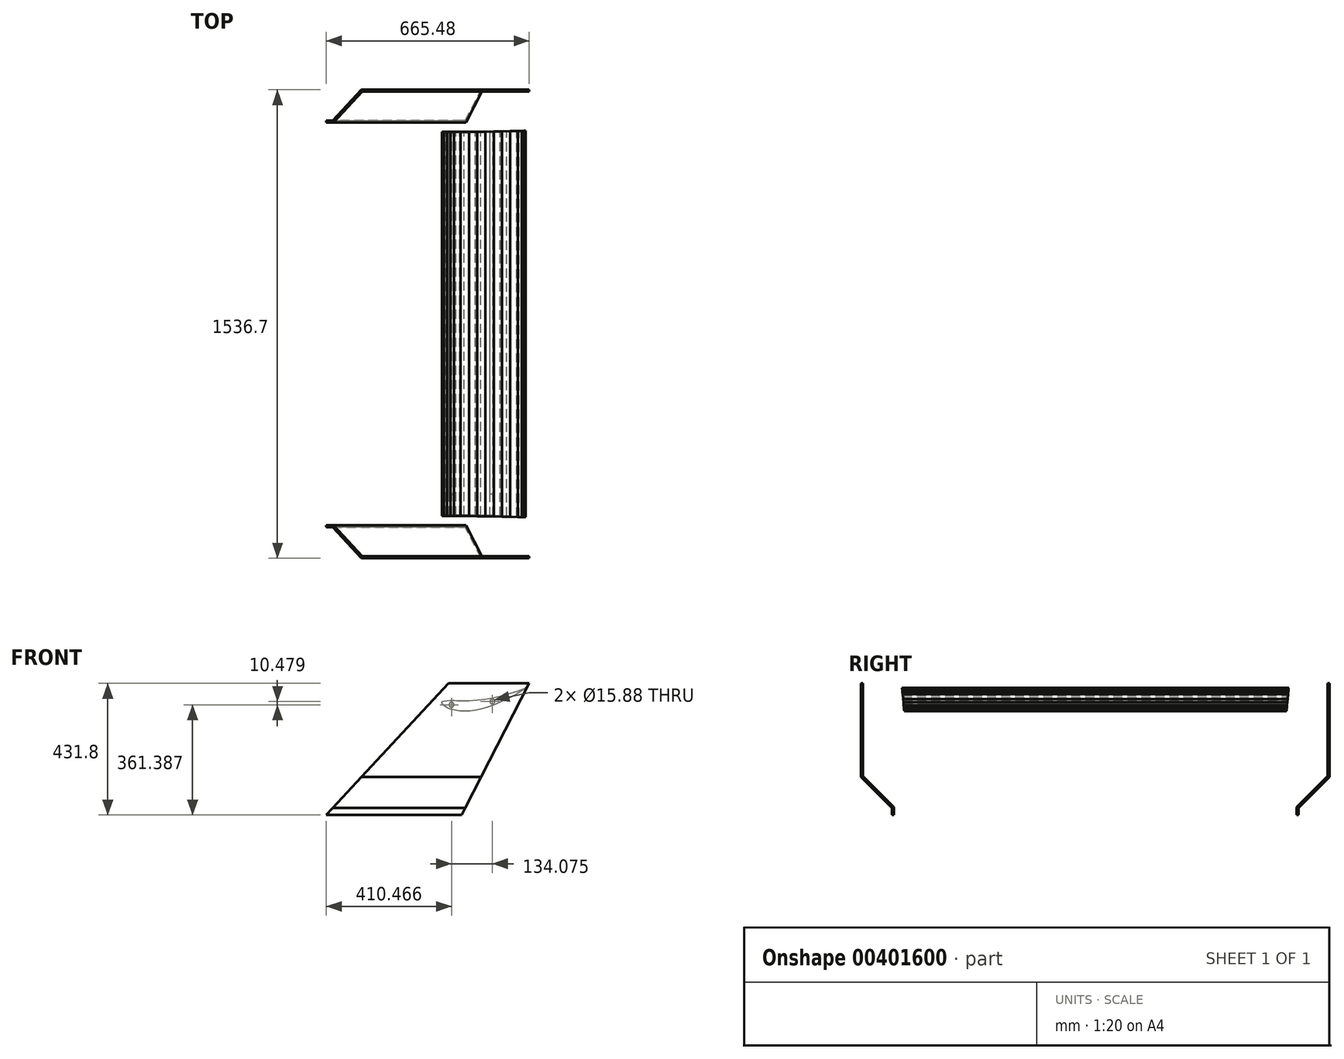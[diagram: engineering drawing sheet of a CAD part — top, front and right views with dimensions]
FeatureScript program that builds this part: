
annotation { "Feature Type Name" : "Feature", "Feature Type Description" : "" }
export const myFeature = defineFeature(function(context is Context, id is Id, definition is map)
    precondition{}
    {
        {
            var Q0;
            Q0=qCreatedBy(makeId("Front.planeOp"),FACE);
            var sketch = newSketch(context, id + "F0", { "sketchPlane" : qUnion([Q0])});
            skLineSegment(sketch, "E0.MirrorCS", {"start": v(175.68, 60.41) * mm, "end": v(175.68, 60.41) * mm});
            skLineSegment(sketch, "E1.MirrorCS", {"start": v(175.68, 60.41) * mm, "end": v(175.68, 60.4) * mm});
            skLineSegment(sketch, "E2.MirrorCS", {"start": v(175.68, 60.4) * mm, "end": v(175.68, 60.4) * mm});
            skLineSegment(sketch, "E3.MirrorCS", {"start": v(175.68, 60.4) * mm, "end": v(175.67, 60.4) * mm});
            skLineSegment(sketch, "E4.MirrorCS", {"start": v(175.67, 60.4) * mm, "end": v(175.63, 60.36) * mm});
            skLineSegment(sketch, "E5.MirrorCS", {"start": v(175.63, 60.36) * mm, "end": v(175.52, 60.28) * mm});
            skLineSegment(sketch, "E6.MirrorCS", {"start": v(175.52, 60.28) * mm, "end": v(175.2, 60.07) * mm});
            skLineSegment(sketch, "E7.MirrorCS", {"start": v(175.2, 60.07) * mm, "end": v(174.57, 59.64) * mm});
            skLineSegment(sketch, "E8.MirrorCS", {"start": v(175.58, 60.37) * mm, "end": v(175.66, 60.4) * mm});
            skLineSegment(sketch, "E9.MirrorCS", {"start": v(174.57, 59.64) * mm, "end": v(173.65, 58.98) * mm});
            skLineSegment(sketch, "E10.MirrorCS", {"start": v(175.22, 60.2) * mm, "end": v(175.58, 60.37) * mm});
            skLineSegment(sketch, "E11.MirrorCS", {"start": v(175.66, 60.4) * mm, "end": v(175.68, 60.41) * mm});
            skLineSegment(sketch, "E12.MirrorCS", {"start": v(174.2, 59.69) * mm, "end": v(175.22, 60.2) * mm});
            skLineSegment(sketch, "E13.MirrorCS", {"start": v(-99.43, 13.1) * mm, "end": v(-99.05, 14.17) * mm});
            skLineSegment(sketch, "E14.MirrorCS", {"start": v(-99.46, 11.96) * mm, "end": v(-99.43, 13.1) * mm});
            skLineSegment(sketch, "E15.MirrorCS", {"start": v(173.65, 58.98) * mm, "end": v(172.07, 57.7) * mm});
            skLineSegment(sketch, "E16.MirrorCS", {"start": v(172.07, 57.7) * mm, "end": v(168.47, 54.76) * mm});
            skLineSegment(sketch, "E17.MirrorCS", {"start": v(169.51, 57.67) * mm, "end": v(172.47, 58.9) * mm});
            skLineSegment(sketch, "E18.MirrorCS", {"start": v(-99.05, 14.17) * mm, "end": v(-97.26, 15.57) * mm});
            skLineSegment(sketch, "E19.MirrorCS", {"start": v(-97.14, 6.38) * mm, "end": v(-98.65, 9.03) * mm});
            skLineSegment(sketch, "E20.MirrorCS", {"start": v(172.47, 58.9) * mm, "end": v(174.2, 59.69) * mm});
            skLineSegment(sketch, "E21.MirrorCS", {"start": v(-97.26, 15.57) * mm, "end": v(-93, 17.2) * mm});
            skLineSegment(sketch, "E22.MirrorCS", {"start": v(-98.65, 9.03) * mm, "end": v(-99.46, 11.96) * mm});
            skLineSegment(sketch, "E23.MirrorCS", {"start": v(-95.22, 4) * mm, "end": v(-97.14, 6.38) * mm});
            skLineSegment(sketch, "E24.MirrorCS", {"start": v(150.15, 50.38) * mm, "end": v(163, 55.07) * mm});
            skLineSegment(sketch, "E25.MirrorCS", {"start": v(-49.22, 18.5) * mm, "end": v(-38.24, 18.2) * mm});
            skLineSegment(sketch, "E26.MirrorCS", {"start": v(-53.7, -13.81) * mm, "end": v(-67.02, -10.8) * mm});
            skLineSegment(sketch, "E27.MirrorCS", {"start": v(68.4, 3.21) * mm, "end": v(45.5, -5.16) * mm});
            skLineSegment(sketch, "E28.MirrorCS", {"start": v(163, 55.07) * mm, "end": v(169.51, 57.67) * mm});
            skLineSegment(sketch, "E29.MirrorCS", {"start": v(168.47, 54.76) * mm, "end": v(161.17, 49.3) * mm});
            skLineSegment(sketch, "E30.MirrorCS", {"start": v(161.17, 49.3) * mm, "end": v(153.4, 44.44) * mm});
            skLineSegment(sketch, "E31.MirrorCS", {"start": v(153.4, 44.44) * mm, "end": v(145.45, 39.92) * mm});
            skCircle(sketch, "E32.MirrorC", {"center": v(-67.77, 4.73) * mm, "radius": 7.94 * mm});
            skCircle(sketch, "E33.MirrorC", {"center": v(66.3, 15.2) * mm, "radius": 7.94 * mm});
            skLineSegment(sketch, "E34.MirrorCS", {"start": v(-38.24, 18.2) * mm, "end": v(-10.8, 18.36) * mm});
            skLineSegment(sketch, "E35.MirrorCS", {"start": v(-67.02, -10.8) * mm, "end": v(-74.67, -8.32) * mm});
            skLineSegment(sketch, "E36.MirrorCS", {"start": v(-82.14, 18.8) * mm, "end": v(-71.16, 19.11) * mm});
            skLineSegment(sketch, "E37.MirrorCS", {"start": v(-8.22, -15.84) * mm, "end": v(-26.5, -16.32) * mm});
            skLineSegment(sketch, "E38.MirrorCS", {"start": v(45.5, -5.16) * mm, "end": v(27.9, -10.16) * mm});
            skLineSegment(sketch, "E39.MirrorCS", {"start": v(16.58, 20.21) * mm, "end": v(43.8, 23.77) * mm});
            skLineSegment(sketch, "E40.MirrorCS", {"start": v(-82.08, -5.17) * mm, "end": v(-89.06, -1.17) * mm});
            skLineSegment(sketch, "E41.MirrorCS", {"start": v(145.45, 39.92) * mm, "end": v(112.94, 23.13) * mm});
            skLineSegment(sketch, "E42.MirrorCS", {"start": v(97.6, 34.6) * mm, "end": v(124.05, 41.9) * mm});
            skLineSegment(sketch, "E43.MirrorCS", {"start": v(-10.8, 18.36) * mm, "end": v(16.58, 20.21) * mm});
            skLineSegment(sketch, "E44.MirrorCS", {"start": v(-74.67, -8.32) * mm, "end": v(-82.08, -5.17) * mm});
            skLineSegment(sketch, "E45.MirrorCS", {"start": v(-71.16, 19.11) * mm, "end": v(-60.19, 18.9) * mm});
            skLineSegment(sketch, "E46.MirrorCS", {"start": v(-26.5, -16.32) * mm, "end": v(-40.15, -15.59) * mm});
            skLineSegment(sketch, "E47.MirrorCS", {"start": v(27.9, -10.16) * mm, "end": v(9.96, -13.76) * mm});
            skLineSegment(sketch, "E48.MirrorCS", {"start": v(43.8, 23.77) * mm, "end": v(70.82, 28.58) * mm});
            skLineSegment(sketch, "E49.MirrorCS", {"start": v(-89.06, -1.17) * mm, "end": v(-95.22, 4) * mm});
            skLineSegment(sketch, "E50.MirrorCS", {"start": v(112.94, 23.13) * mm, "end": v(90.85, 12.77) * mm});
            skLineSegment(sketch, "E51.MirrorCS", {"start": v(124.05, 41.9) * mm, "end": v(150.15, 50.38) * mm});
            skLineSegment(sketch, "E52.MirrorCS", {"start": v(-60.19, 18.9) * mm, "end": v(-49.22, 18.5) * mm});
            skLineSegment(sketch, "E53.MirrorCS", {"start": v(-40.15, -15.59) * mm, "end": v(-53.7, -13.81) * mm});
            skLineSegment(sketch, "E54.MirrorCS", {"start": v(9.96, -13.76) * mm, "end": v(-8.22, -15.84) * mm});
            skLineSegment(sketch, "E55.MirrorCS", {"start": v(70.82, 28.58) * mm, "end": v(97.6, 34.6) * mm});
            skLineSegment(sketch, "E56.MirrorCS", {"start": v(90.85, 12.77) * mm, "end": v(68.4, 3.21) * mm});
            skLineSegment(sketch, "E57.MirrorCS", {"start": v(-93, 17.2) * mm, "end": v(-82.14, 18.8) * mm});
            skSolve(sketch);
        }
        {
            var Q0;
            Q0 = qSketchRegion(id + "F0", true);
            extrude(context, id + "F1", {"entities" : qUnion([Q0]), "depth" : 1524 * mm});
        }
        {
            var Q0;
            Q0=makeQuery(id+"F0.imprint","IMPRINT",FACE,{"disambiguationData":[TD([[makeQuery(id+"F0.imprint","IMPRINT",EDGE,{"derivedFrom":sQuery(id+"F0.wireOp",EDGE,"E32.MirrorC")}),1.0]])]});
            var Q1;
            Q1=makeQuery(id+"F0.imprint","IMPRINT",FACE,{"disambiguationData":[TD([[makeQuery(id+"F0.imprint","IMPRINT",EDGE,{"derivedFrom":sQuery(id+"F0.wireOp",EDGE,"E33.MirrorC")}),1.0]])]});
            extrude(context, id + "F2", {"entities" : qUnion([Q0, Q1]), "depth" : 1320.8 * mm});
        }
        {
            var Q0;
            Q0=qCreatedBy(makeId("Front.planeOp"),FACE);
            var sketch = newSketch(context, id + "F3", { "sketchPlane" : qUnion([Q0])});
            skLineSegment(sketch, "E58", {"start": v(187.24, 75.14) * mm, "end": v(-77.3, 75.14) * mm});
            skLineSegment(sketch, "E59", {"start": v(-90.12, -356.66) * mm, "end": v(-195.44, -356.66) * mm});
            skLineSegment(sketch, "E60", {"start": v(-195.44, -356.66) * mm, "end": v(-33.97, -356.66) * mm});
            skLineSegment(sketch, "E61", {"start": v(-142.78, -356.66) * mm, "end": v(-257.43, -356.66) * mm});
            skLineSegment(sketch, "E62", {"start": v(-190.28, -356.66) * mm, "end": v(-320.78, -356.66) * mm});
            skLineSegment(sketch, "E63", {"start": v(-276.1, -356.66) * mm, "end": v(-478.24, -356.66) * mm});
            skLineSegment(sketch, "E64", {"start": v(-77.3, 75.14) * mm, "end": v(-478.24, -356.66) * mm});
            skLineSegment(sketch, "E65", {"start": v(187.24, 75.14) * mm, "end": v(-33.97, -356.66) * mm});
            skPoint(sketch, "E66.orphan", {"position": v(0, -356.66) * mm});
            skSolve(sketch);
        }
        {
            var Q0;
            Q0 = qSketchRegion(id + "F3", true);
            extrude(context, id + "F4", {"entities" : qUnion([Q0]), "oppositeDirection" : true, "depth" : 6.35 * mm, "hasSecondDirection" : true, "secondDirectionOppositeDirection" : false, "secondDirectionDepth" : 101.6 * mm});
        }
        {
            var Q0;
            Q0 = qSketchRegion(id + "F3", true);
            extrude(context, id + "F5", {"entities" : qUnion([Q0]), "depth" : 1530.35 * mm, "hasSecondDirection" : true, "secondDirectionOppositeDirection" : false, "secondDirectionDepth" : 1422.4 * mm});
        }
        {
            var Q0;
            Q0=makeQuery(id+"F5.opExtrude","CAP_FACE",FACE,{"disambiguationData":[OSD([sQuery(id+"F3.wireOp",EDGE,"E58"),sQuery(id+"F3.wireOp",EDGE,"hNdFN1td-OKNO-mdAZ-5iT6-GzoFEjob44qA"),sQuery(id+"F3.wireOp",EDGE,"E60"),sQuery(id+"F3.wireOp",EDGE,"ngflrQah-cpfp-qguv-KpUv-2jsHnshwBWnx")])],"isStart":false});
            var sketch = newSketch(context, id + "F6", { "sketchPlane" : qUnion([Q0])});
            skCircle(sketch, "E67", {"center": v(-51.48, 2.54) * mm, "radius": 3.17 * mm});
            skCircle(sketch, "E68", {"center": v(108.72, 29.95) * mm, "radius": 3.18 * mm});
            skSolve(sketch);
        }
        {
            var Q0;
            Q0 = qSketchRegion(id + "F6", true);
            extrude(context, id + "F7", {"entities" : qUnion([Q0]), "operationType" : NewBodyOperationType.REMOVE, "oppositeDirection" : true, "depth" : 25.4 * mm});
        }
        {
            var Q0;
            Q0 = qSketchRegion(id + "F6", true);
            extrude(context, id + "F8", {"entities" : qUnion([Q0]), "operationType" : NewBodyOperationType.REMOVE, "oppositeDirection" : true, "depth" : 1333.5 * mm, "hasSecondDirection" : true, "secondDirectionOppositeDirection" : true, "secondDirectionDepth" : 1308.1 * mm});
        }
        {
            var Q0;
            Q0 = qSketchRegion(id + "F6", true);
            extrude(context, id + "F9", {"entities" : qUnion([Q0]), "oppositeDirection" : true, "depth" : 25.4 * mm});
        }
        {
            var Q0;
            Q0=makeQuery(id+"F5.opExtrude","CAP_FACE",FACE,{"disambiguationData":[OSD([sQuery(id+"F3.wireOp",EDGE,"E58"),sQuery(id+"F3.wireOp",EDGE,"hNdFN1td-OKNO-mdAZ-5iT6-GzoFEjob44qA"),sQuery(id+"F3.wireOp",EDGE,"E60"),sQuery(id+"F3.wireOp",EDGE,"ngflrQah-cpfp-qguv-KpUv-2jsHnshwBWnx")])],"isStart":false});
            var sketch = newSketch(context, id + "F10", { "sketchPlane" : qUnion([Q0])});
            skCircle(sketch, "E69", {"center": v(-51.48, 2.54) * mm, "radius": 6.35 * mm});
            skCircle(sketch, "E70", {"center": v(108.72, 29.95) * mm, "radius": 6.35 * mm});
            skSolve(sketch);
        }
        {
            var Q0;
            Q0 = qSketchRegion(id + "F6", true);
            extrude(context, id + "F11", {"entities" : qUnion([Q0]), "oppositeDirection" : true, "depth" : 1333.5 * mm, "hasSecondDirection" : true, "secondDirectionOppositeDirection" : true, "secondDirectionDepth" : 1308.1 * mm});
        }
        {
            var Q0;
            Q0 = qSketchRegion(id + "F10", true);
            extrude(context, id + "F12", {"entities" : qUnion([Q0]), "operationType" : NewBodyOperationType.ADD, "depth" : 2.54 * mm});
        }
        {
            var Q0;
            Q0 = qSketchRegion(id + "F10", true);
            extrude(context, id + "F13", {"entities" : qUnion([Q0]), "operationType" : NewBodyOperationType.ADD, "oppositeDirection" : true, "depth" : 1336.04 * mm, "hasSecondDirection" : true, "secondDirectionOppositeDirection" : true, "secondDirectionDepth" : 1333.5 * mm});
        }
        {
            var Q0;
            Q0=makeQuery(id+"F13.opExtrude","CAP_EDGE",EDGE,{"disambiguationData":[OSD([sQuery(id+"F10.wireOp",EDGE,"E70")])],"isStart":false});
            var Q1;
            Q1=makeQuery(id+"F13.opExtrude","CAP_EDGE",EDGE,{"disambiguationData":[OSD([sQuery(id+"F10.wireOp",EDGE,"E69")])],"isStart":false});
            var Q2;
            Q2=makeQuery(id+"F12.opExtrude","CAP_EDGE",EDGE,{"disambiguationData":[OSD([sQuery(id+"F10.wireOp",EDGE,"E70")])],"isStart":false});
            var Q3;
            Q3=makeQuery(id+"F12.opExtrude","CAP_EDGE",EDGE,{"disambiguationData":[OSD([sQuery(id+"F10.wireOp",EDGE,"E69")])],"isStart":false});
            fillet(context, id + "F14", {"entities" : qUnion([Q0, Q1, Q2, Q3]), "radius" : 5.08 * mm, "tangentPropagation" : true, "allowEdgeOverflow" : false});
        }
        {
            var Q0;
            Q0=qCreatedBy(makeId("Right.planeOp"),FACE);
            var sketch = newSketch(context, id + "F15", { "sketchPlane" : qUnion([Q0])});
            skLineSegment(sketch, "E71", {"start": v(0, 75.14) * mm, "end": v(0, -229.66) * mm});
            skLineSegment(sketch, "E72", {"start": v(6.35, 75.14) * mm, "end": v(6.35, -229.66) * mm});
            skLineSegment(sketch, "E73", {"start": v(0, -229.66) * mm, "end": v(-101.6, -331.26) * mm});
            skLineSegment(sketch, "E74", {"start": v(-101.6, -356.66) * mm, "end": v(-101.6, -331.26) * mm});
            skLineSegment(sketch, "E75", {"start": v(6.35, -232.29) * mm, "end": v(-95.25, -333.89) * mm});
            skLineSegment(sketch, "E76", {"start": v(-95.25, -356.66) * mm, "end": v(-95.25, -333.89) * mm});
            skLineSegment(sketch, "E77", {"start": v(6.35, 75.14) * mm, "end": v(6.35, -232.29) * mm});
            skLineSegment(sketch, "E78", {"start": v(-95.25, -356.66) * mm, "end": v(-95.25, -413.25) * mm});
            skLineSegment(sketch, "E79", {"start": v(-95.25, -413.25) * mm, "end": v(70.88, -417.63) * mm});
            skLineSegment(sketch, "E80", {"start": v(70.88, -417.63) * mm, "end": v(100, 126) * mm});
            skLineSegment(sketch, "E81", {"start": v(100, 126) * mm, "end": v(13.66, 114.46) * mm});
            skLineSegment(sketch, "E82", {"start": v(13.66, 114.46) * mm, "end": v(6.35, 75.14) * mm});
            skLineSegment(sketch, "E83", {"start": v(0, 75.14) * mm, "end": v(-14.18, 112.35) * mm});
            skLineSegment(sketch, "E84", {"start": v(-14.18, 112.35) * mm, "end": v(-123.83, 107.8) * mm});
            skLineSegment(sketch, "E85", {"start": v(-123.83, 107.8) * mm, "end": v(-169.23, -395.81) * mm});
            skLineSegment(sketch, "E86", {"start": v(-169.23, -395.81) * mm, "end": v(-101.6, -356.66) * mm});
            skLineSegment(sketch, "E87", {"start": v(-762, 196.4) * mm, "end": v(-762, -337.2) * mm});
            skLineSegment(sketch, "E88.MirrorCS", {"start": v(-1624, 126) * mm, "end": v(-1537.66, 114.46) * mm});
            skLineSegment(sketch, "E89.MirrorCS", {"start": v(-1537.66, 114.46) * mm, "end": v(-1530.35, 75.14) * mm});
            skLineSegment(sketch, "E90.MirrorCS", {"start": v(-1530.35, 75.14) * mm, "end": v(-1530.35, -232.29) * mm});
            skLineSegment(sketch, "E91.MirrorCS", {"start": v(-1594.88, -417.63) * mm, "end": v(-1624, 126) * mm});
            skLineSegment(sketch, "E92.MirrorCS", {"start": v(-1428.75, -413.25) * mm, "end": v(-1594.88, -417.63) * mm});
            skLineSegment(sketch, "E93.MirrorCS", {"start": v(-1428.75, -356.66) * mm, "end": v(-1428.75, -413.25) * mm});
            skLineSegment(sketch, "E94.MirrorCS", {"start": v(-1428.75, -356.66) * mm, "end": v(-1428.75, -333.89) * mm});
            skLineSegment(sketch, "E95.MirrorCS", {"start": v(-1530.35, -232.29) * mm, "end": v(-1428.75, -333.89) * mm});
            skLineSegment(sketch, "E96.MirrorCS", {"start": v(-1524, 75.14) * mm, "end": v(-1524, -229.66) * mm});
            skLineSegment(sketch, "E97.MirrorCS", {"start": v(-1524, 75.14) * mm, "end": v(-1509.82, 112.35) * mm});
            skLineSegment(sketch, "E98.MirrorCS", {"start": v(-1509.82, 112.35) * mm, "end": v(-1400.17, 107.8) * mm});
            skLineSegment(sketch, "E99.MirrorCS", {"start": v(-1400.17, 107.8) * mm, "end": v(-1354.77, -395.81) * mm});
            skLineSegment(sketch, "E100.MirrorCS", {"start": v(-1354.77, -395.81) * mm, "end": v(-1422.4, -356.66) * mm});
            skLineSegment(sketch, "E101.MirrorCS", {"start": v(-1422.4, -356.66) * mm, "end": v(-1422.4, -331.26) * mm});
            skLineSegment(sketch, "E102.MirrorCS", {"start": v(-1524, -229.66) * mm, "end": v(-1422.4, -331.26) * mm});
            skSolve(sketch);
        }
        {
            var Q0;
            Q0 = qSketchRegion(id + "F15", true);
            extrude(context, id + "F16", {"entities" : qUnion([Q0]), "operationType" : NewBodyOperationType.REMOVE, "oppositeDirection" : true, "depth" : 1480.82 * mm, "hasSecondDirection" : true, "secondDirectionOppositeDirection" : false, "secondDirectionDepth" : 828.04 * mm});
        }
    });
